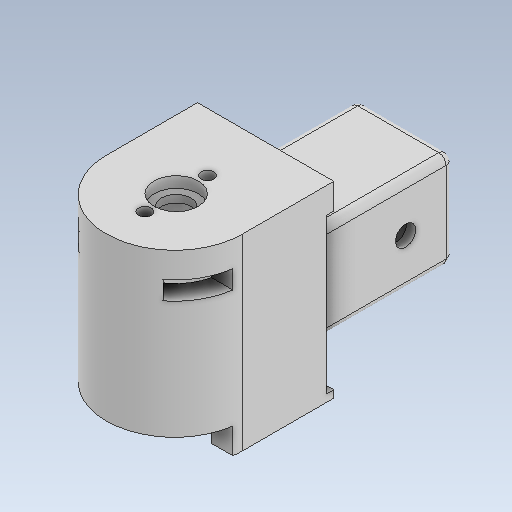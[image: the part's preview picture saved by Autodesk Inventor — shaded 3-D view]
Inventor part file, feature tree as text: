
AUTODESK INVENTOR PART (.ipt)
format: ipt  version: 2020.2 (Build 242310000, 310)  size: 445,952 bytes
history: native  units: mm
features: sketch x16, extrude x11, hole x5, fillet x4
ambient origin geometry x8: Origin, YZ Plane, XZ Plane, XY Plane, X Axis, Y Axis, Z Axis, Center Point
bodies: Solido1 (feature_tree)
feature tree (36):
  extrude  "Estrusione1"  Depth=18.0mm
  extrude  "Estrusione2"  Depth=40.0mm TaperAngle=0.0deg
  extrude  "Estrusione3"  Depth=46.0mm
  extrude  "Estrusione7"  Depth=37.0mm
  extrude  "Estrusione8"  Depth=21.0mm TaperAngle=0.0deg
  extrude  "Estrusione10"  Depth=22.5mm
  hole  "Foro4"  [1 undecoded]
  hole  "Foro5"  [1 undecoded]
  fillet  "Raccordo1"  Radius=46.0mm
  fillet  "Raccordo2"  Radius=37.0mm
  fillet  "Raccordo3"  Radius=37.0mm
  sketch  "Schizzo17"
  extrude  "Estrusione11"  Depth=14.0mm
  extrude  "Estrusione12"  TaperAngle=90.0deg  [1 undecoded]
  hole  "Foro6"  [1 undecoded]
  hole  "Foro7"  [1 undecoded]
  hole  "Foro8"  [1 undecoded]
  extrude  "Estrusione13"  Depth=14.0mm
  extrude  "Estrusione14"  TaperAngle=180.0deg  [1 undecoded]
  extrude  "Estrusione15"  TaperAngle=90.0deg  [1 undecoded]
  fillet  "Raccordo4"  Radius=21.0mm
  sketch  "Schizzo1"
  sketch  "Schizzo2"
  sketch  "Schizzo3"
  sketch  "Schizzo7"
  sketch  "Schizzo8"
  sketch  "Schizzo14"
  sketch  "Schizzo15"
  sketch  "Schizzo16"
  sketch  "Schizzo18"
  sketch  "Schizzo19"
  sketch  "Schizzo21"
  sketch  "Schizzo22"
  sketch  "Schizzo23"
  sketch  "Schizzo24"
  sketch  "Schizzo25"
note: 8 required parameter values undecoded (feature->parameter linkage not recoverable at this tier; creation-order binding heuristic only, values carry confidence <= 0.55)
